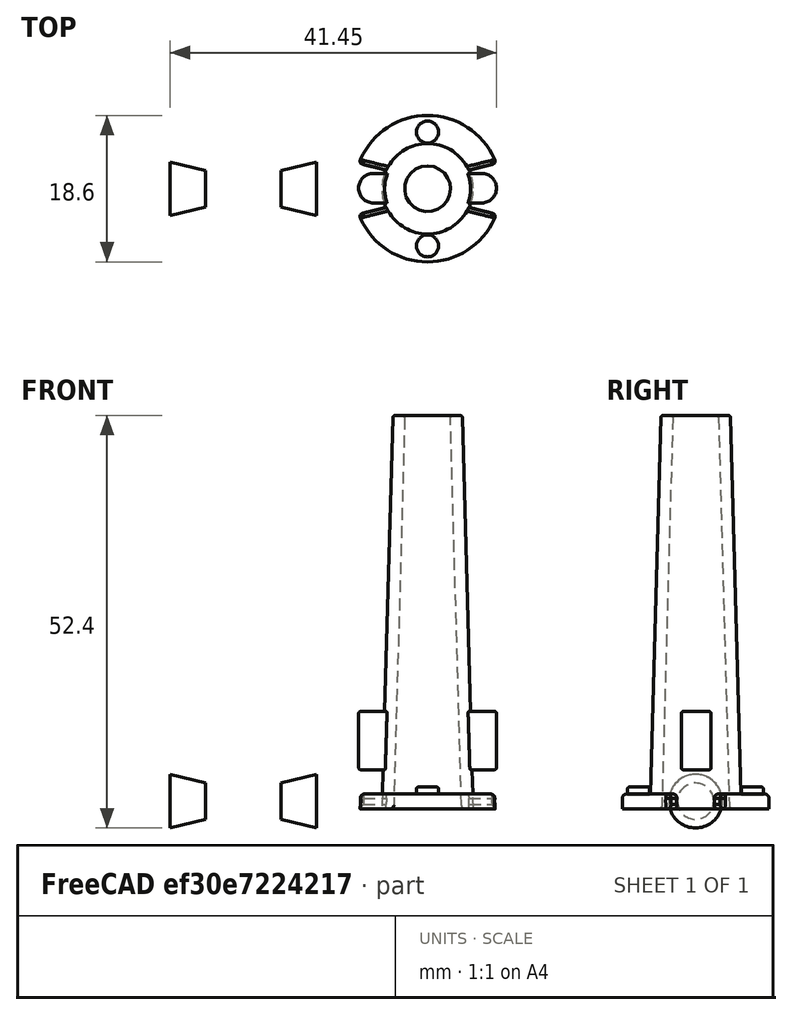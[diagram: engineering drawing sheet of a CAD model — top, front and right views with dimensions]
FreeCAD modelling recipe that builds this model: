
FCSTD DOCUMENT  (FreeCAD 0.19R21938 (Git))
Label: Launch Pad Pin
License: All rights reserved
LicenseURL: http://en.wikipedia.org/wiki/All_rights_reserved
objects: Part::Fillet×8, Part::Cone×5, Part::Cylinder×3, Part::Cut×3, Part::MultiFuse×3, App::LinkGroup×2, Part::Box×1
note: 23 computed .brp shape members not serialized (recipe doc carries the construction recipe); baked Part::Feature solids carry a one-line shape summary decoded from their .brp

FEATURE [Part::Cone] Cone  label="Outer"
  Angle = 360
  AttacherType = Attacher::AttachEngine3D
  Height = 50
  Radius1 = 5.8
  Radius2 = 4.4
FEATURE [Part::Cone] Cone001  label="Inner"
  Angle = 360
  AttacherType = Attacher::AttachEngine3D
  Height = 50
  Radius1 = 4.3
  Radius2 = 2.9
FEATURE [Part::Cylinder] Cylinder
  Angle = 360
  AttacherType = Attacher::AttachEngine3D
  Height = 1.9
  Radius = 9.3
FEATURE [Part::Cone] Cone002  label="Cone"
  Angle = 360
  AttacherType = Attacher::AttachEngine3D
  Height = 4.5
  Placement = pos=(-28.2,0,1) rot=(0,-1,0;1.5708rad)
  Radius1 = 2.3
  Radius2 = 3.4
FEATURE [Part::Cone] Cone003  label="Outer001"
  Angle = 360
  AttacherType = Attacher::AttachEngine3D
  Height = 50
  Placement = pos=(-23.4,0,0) rot=(0,0,1;0rad)
  Radius1 = 5.8
  Radius2 = 4.4
FEATURE [Part::Cone] Cone004
  Angle = 360
  AttacherType = Attacher::AttachEngine3D
  Height = 4.5
  Placement = pos=(-18.6,-1e-15,1) rot=(0.707107,0,0.707107;3.14159rad)
  Radius1 = 2.3
  Radius2 = 3.4
FEATURE [App::LinkGroup] LinkGroup
  ElementList = -> [Cone002,Cone004]
  LinkMode = 0
FEATURE [Part::Cut] Cut001
  Base = -> LinkGroup
  Placement = pos=(23.4,0,0) rot=(0,0,1;0rad)
  Tool = -> Cone003
FEATURE [Part::Cut] Cut002
  Base = -> Cylinder
  Tool = -> Cut001
FEATURE [Part::Box] Box  label="Cube"
  AttacherType = Attacher::AttachEngine3D
  Height = 7.4
  Length = 17.5
  Placement = pos=(-8.75,-1.8,3.1) rot=(0,0,1;0rad)
  Width = 3.75
FEATURE [Part::Fillet] Fillet004
  Base = -> Box
  Edges = 2 edges r=1.87: [Edge5,Edge7]
FEATURE [Part::Fillet] Fillet005
  Base = -> Fillet004
  Edges = 2 edges r=1.87: [Edge17,Edge18]
  Placement = pos=(0,0,1.9) rot=(0,0,1;0rad)
FEATURE [Part::Cylinder] Cylinder001
  Angle = 360
  AttacherType = Attacher::AttachEngine3D
  Height = 1
  Placement = pos=(-0.0063,-7.25,1.8) rot=(0,0,1;0rad)
  Radius = 1.4
FEATURE [Part::Cylinder] Cylinder002
  Angle = 360
  AttacherType = Attacher::AttachEngine3D
  Height = 1
  Placement = pos=(-0.0063,7.2,1.8) rot=(0,0,1;0rad)
  Radius = 1.4
FEATURE [Part::Fillet] Fillet006
  Base = -> Cylinder001
  Edges = 1 edges r=0.25: [Edge1]
FEATURE [Part::Fillet] Fillet007
  Base = -> Cylinder002
  Edges = 1 edges r=0.25: [Edge1]
FEATURE [App::LinkGroup] LinkGroup001  label="Keeper PIns"
  ElementList = -> [Fillet006,Fillet007]
  LinkMode = 0
FEATURE [Part::Fillet] Fillet  label="Hold PIns"
  Base = -> Fillet005
  Edges = 12 edges r=0.25: [Edge1,Edge2,Edge4,Edge5,Edge6,Edge8,Edge9,Edge12,Edge14,Edge20,Edge22,Edge24]
FEATURE [Part::Fillet] Fillet008
  Base = -> Cut002
  Edges = 16 edges r=0.5: [Edge1,Edge2,Edge4,Edge5,Edge6,Edge7,Edge9,Edge13,Edge17,Edge20,Edge21,Edge25,Edge26,Edge30,Edge33,Edge34]
FEATURE [Part::MultiFuse] Fusion
  Shapes = -> [Cone,Fillet008]
FEATURE [Part::MultiFuse] Fusion001
  Shapes = -> [Fillet,Fusion]
FEATURE [Part::MultiFuse] Fusion002
  Shapes = -> [LinkGroup001,Fusion001]
FEATURE [Part::Cut] Cut
  Base = -> Fusion002
  Tool = -> Cone001
FEATURE [Part::Fillet] Fillet009
  Base = -> Cut
  Edges = 1 edges r=0.5: [Edge133]
FEATURE [Part::Fillet] Fillet010  label="Pin"
  Base = -> Fillet009
  Edges = 2 edges r=0.25: [Edge46,Edge56]
